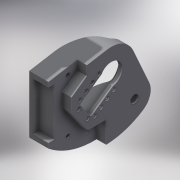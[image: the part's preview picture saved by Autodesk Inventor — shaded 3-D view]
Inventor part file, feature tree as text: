
AUTODESK INVENTOR PART (.ipt)
format: ipt  version: 2017 (Build 210142000, 142)  size: 395,264 bytes
history: native  units: mm
features: sketch x11, extrude x9, projected_geometry x4, hole x3, fillet x3, chamfer x1
ambient origin geometry x8: Origin, YZ Plane, XZ Plane, XY Plane, X Axis, Y Axis, Z Axis, Center Point
bodies: Solid1 (feature_tree)
feature tree (31):
  extrude  "Extrusion1"  Depth=22.8mm
  extrude  "Extrusion2"  Depth=20.5mm
  extrude  "Extrusion3"  Depth=30.0mm TaperAngle=0.0deg
  extrude  "Extrusion4"  Depth=14.0mm
  extrude  "Extrusion5"  Depth=34.0mm
  hole  "Hole1"  [1 undecoded]
  fillet  "Fillet1"  Radius=33.583mm
  fillet  "Fillet2"  Radius=16.7915mm
  extrude  "Extrusion6"  Depth=26.0mm TaperAngle=0.0deg
  hole  "Hole2"  [1 undecoded]
  extrude  "Extrusion7"  Depth=17.0mm
  fillet  "Fillet3"  Radius=24.0mm
  extrude  "Extrusion8"  Depth=13.5mm
  extrude  "Extrusion9"  Depth=2.0mm
  hole  "Hole3"  [1 undecoded]
  chamfer  "Chamfer1"  Distance=8.0mm
  sketch  "Sketch1"  dims[d3=30.0mm d4=0.0mm d6=22.8mm]
  sketch  "Sketch2"  dims[d8=9.560914mm d9=20.5mm]
  sketch  "Sketch3"  dims[d10=33.0mm d11=30.0mm d12=0.0mm]
  projected_geometry  "Projected Loop1"
  sketch  "Sketch4"  dims[d14=55.305mm d15=14.0mm]
  sketch  "Sketch5"  dims[d16=17.0mm d17=34.0mm]
  sketch  "Sketch6"  dims[d18=24.0mm d19=25.0mm d20=33.583mm d21=16.7915mm]
  projected_geometry  "Projected Loop2"
  sketch  "Sketch7"  dims[d22=39.541mm d23=26.0mm d24=0.0mm]
  projected_geometry  "Projected Loop3"
  sketch  "Sketch8"  dims[d25=60.0mm d26=30.0mm]
  projected_geometry  "Projected Loop4"
  sketch  "Sketch9"  dims[d27=24.0mm d28=0.0mm d29=17.0mm d30=24.0mm d31=0.0mm]
  sketch  "Sketch10"  dims[d32=13.5mm d33=13.5mm]
  sketch  "Sketch11"  dims[d34=3.0mm d35=6.5mm d36=40.0mm d38=8.0mm d39=20.0mm d41=27.0mm d44=8.0mm d45=2.2mm d46=6.0mm d47=4.2mm d48=1.2mm d49=90.0deg d50=8.0mm d51=20.594885mm d52=2.0mm d53=8.0mm d54=10.0mm d55=0.0mm d56=14.0mm d57=24.0mm d58=50.0mm d59=30.0mm d60=14.0mm d62=20.0mm d63=5.0mm d64=55.0mm d65=26.0mm d66=20.0mm d67=4.2mm d68=6.0mm d69=7.2mm d70=10.0mm d71=90.0deg d72=8.0mm d73=20.594885mm d74=25.295125mm d75=6.14705mm d76=21.855013mm d77=50.0mm d78=16.0mm d79=6.0mm d80=0.0mm d81=3.0mm d82=4.75mm d83=12.0mm d84=1.0mm d85=0.0mm d86=8.0mm d87=7.0mm d88=0.0mm d89=10.0mm d90=10.0mm d91=4.2mm d92=6.0mm d93=8.0mm d94=4.0mm d95=90.0deg d96=8.0mm d97=20.594885mm d98=0.5mm d99=2.0mm d100=45.0deg d101=25.0mm]
note: 3 required parameter values undecoded (feature->parameter linkage not recoverable at this tier; creation-order binding heuristic only, values carry confidence <= 0.55)
